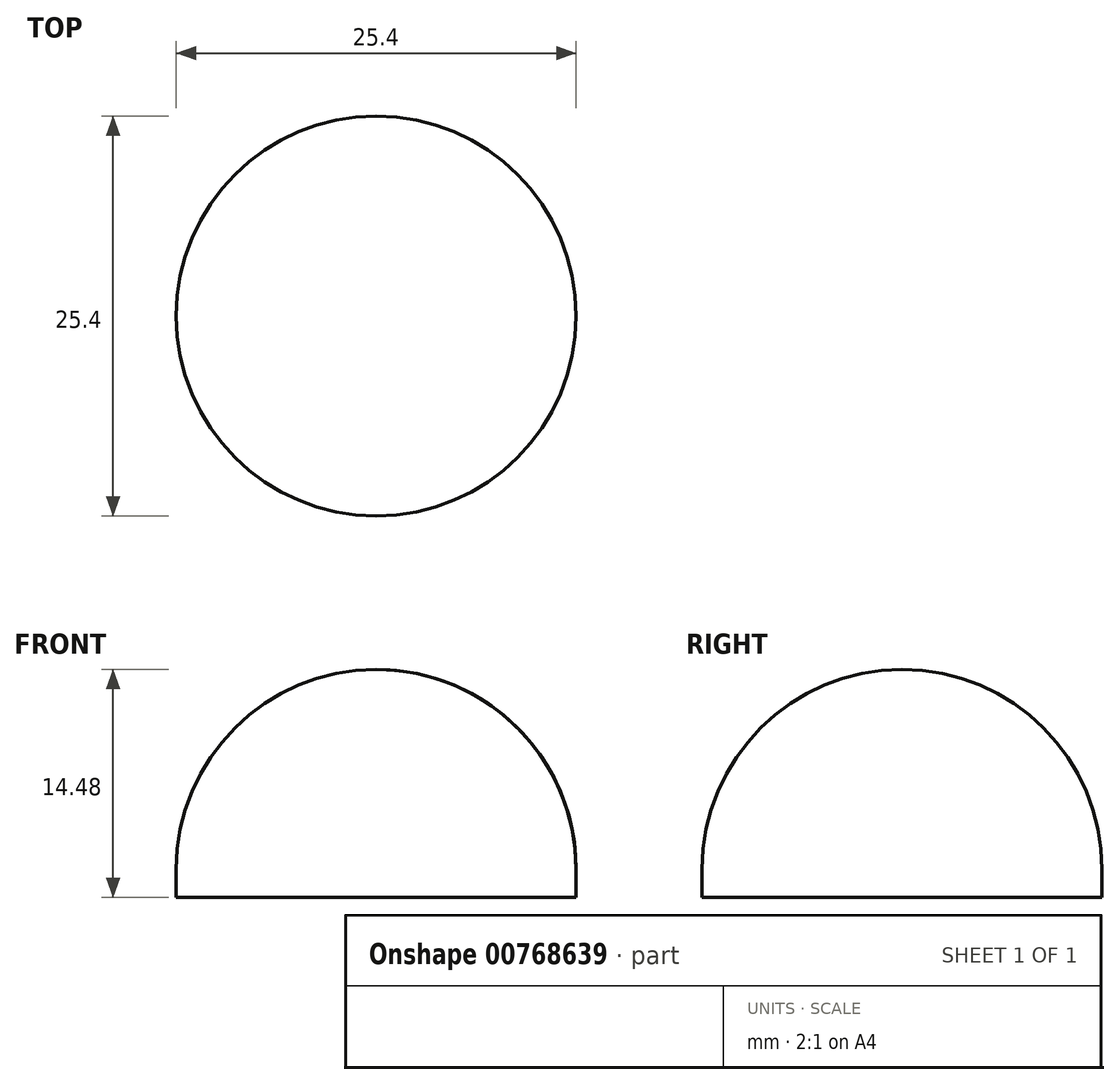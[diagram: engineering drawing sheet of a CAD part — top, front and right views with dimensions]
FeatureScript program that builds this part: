
annotation { "Feature Type Name" : "Feature", "Feature Type Description" : "" }
export const myFeature = defineFeature(function(context is Context, id is Id, definition is map)
    precondition{}
    {
        {
            var Q0;
            Q0=qCreatedBy(makeId("Top.planeOp"),FACE);
            var sketch = newSketch(context, id + "F0", { "sketchPlane" : qUnion([Q0])});
            skCircle(sketch, "E0", {"center": v(-47.35, 36.05) * mm, "radius": 13.97 * mm});
            skCircle(sketch, "E1", {"center": v(-47.35, 36.05) * mm, "radius": 12.7 * mm});
            skSolve(sketch);
        }
        {
            var Q0;
            Q0=makeQuery(id+"F0.imprint","IMPRINT",FACE,{"disambiguationData":[TD([[makeQuery(id+"F0.imprint","IMPRINT",EDGE,{"derivedFrom":sQuery(id+"F0.wireOp",EDGE,"E1")}),1.0]])]});
            extrude(context, id + "F1", {"entities" : qUnion([Q0]), "depth" : 11.94 * mm, "offsetDistance" : 25.4 * mm, "hasSecondDirection" : true, "secondDirectionOppositeDirection" : true, "secondDirectionDepth" : 2.54 * mm});
        }
        {
            var Q0;
            Q0=makeQuery(id+"F1.opExtrude","CAP_EDGE",EDGE,{"disambiguationData":[OSD([sQuery(id+"F0.wireOp",EDGE,"E1")])],"isStart":false});
            fillet(context, id + "F2", {"entities" : qUnion([Q0]), "radius" : 12.7 * mm, "tangentPropagation" : true, "allowEdgeOverflow" : false});
        }
        {
            var Q0;
            Q0=makeQuery(id+"F1.opExtrude","CAP_FACE",FACE,{"disambiguationData":[OSD([sQuery(id+"F0.wireOp",EDGE,"E1")])],"isStart":true});
            extrude(context, id + "F3", {"entities" : qUnion([Q0]), "operationType" : NewBodyOperationType.ADD, "oppositeDirection" : true, "depth" : 0.25 * mm, "offsetDistance" : 25.4 * mm});
        }
    });
